# Revit family: Alcon-15233-2-4-Revit-Family
name_source: partatom
category: Lighting Fixtures
units: mm (PartAtom-declared; Revit-internal decimal feet)

## family parameters
Always vertical = Yes
Cut with Voids When Loaded = No
Host = Ceiling
Light Source = Yes
Part Type = Normal
Room Calculation Point = No
Round Connector Dimension = Use Diameter
Shared = No

## types (4) — shared parameters
Color Filter = 16777215
Default Elevation = 0' - 0"
Dimming Lamp Color Temperature Shift = <None>
Housing = Default
Led Source = Led Source
Lens = Lens
Light Source Symbol Size = 2' - 0"
Link To Product Page = https://www.alconlighting.com
Manufacturer = Alcon Light
Reflector = Reflector

## per-type parameters (varying)
| type | Emit from Line Length | Length | Product Identity |
| 15233-2 - 8FT | 8' - 0" | 8' - 0" | Alcon Lighting 15233-2 |
| 15233-2 - 4FT | 4' - 0" | 4' - 0" | Alcon Lighting 15233-2-4 |
| 15233-2 - 3FT | 3' - 0" | 3' - 0" | Alcon Lighting 15233-2 |
| 15233-2 - 2FT | 2' - 0" | 2' - 0" | Alcon Lighting 15233-2 |

## geometry (parser evidence)
native form markers: Sweep x1
no freeform markers — native parametric forms only
